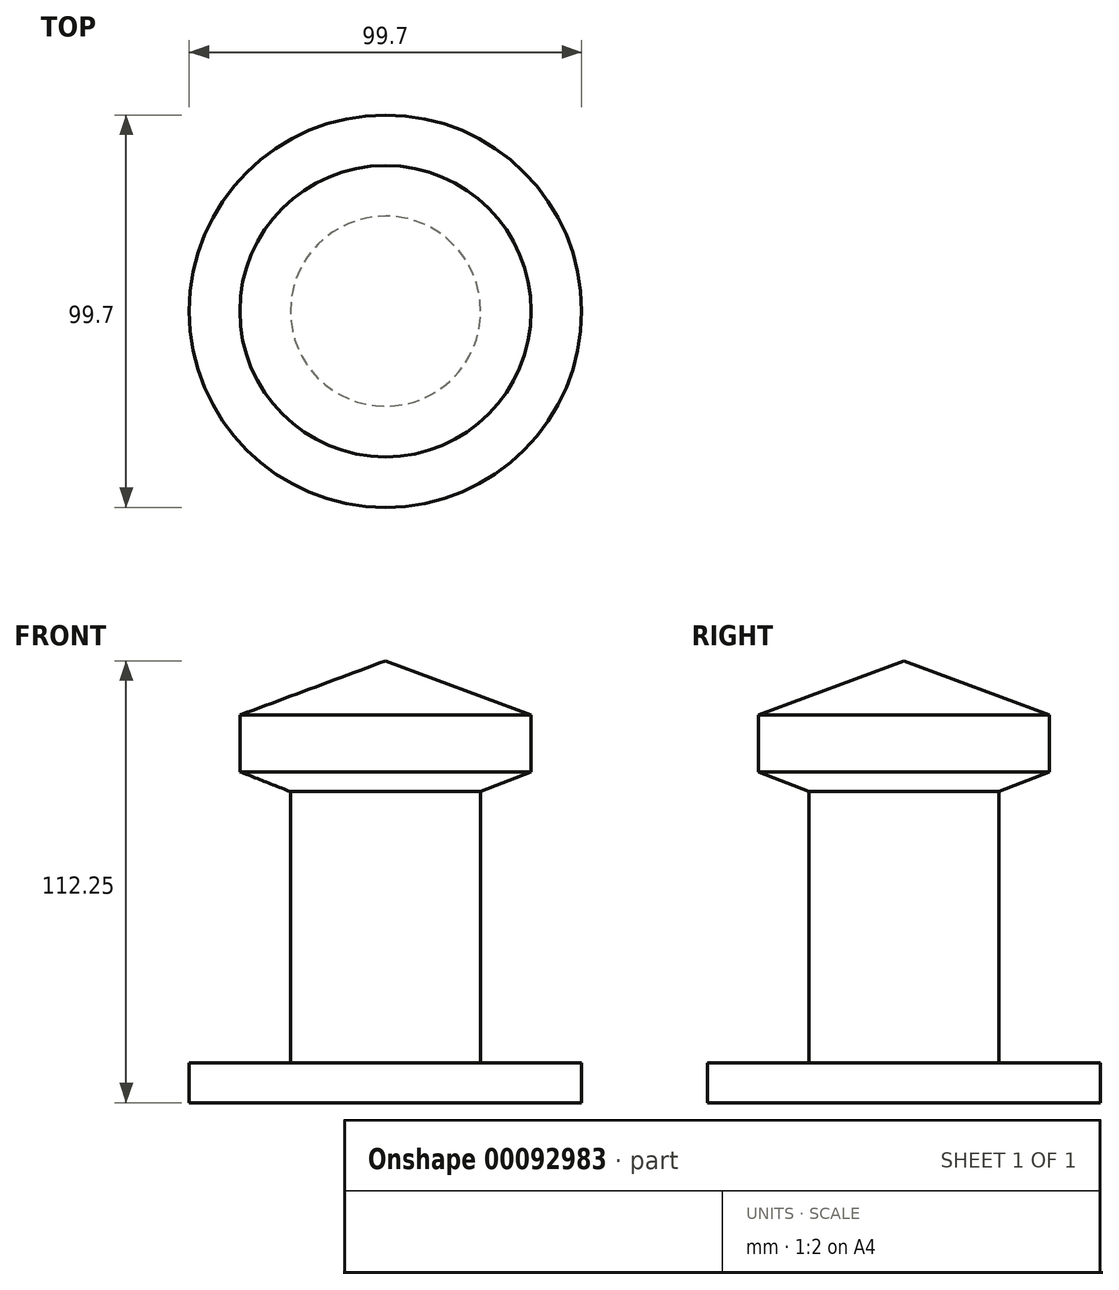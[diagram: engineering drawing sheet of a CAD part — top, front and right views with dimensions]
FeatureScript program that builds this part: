
annotation { "Feature Type Name" : "Feature", "Feature Type Description" : "" }
export const myFeature = defineFeature(function(context is Context, id is Id, definition is map)
    precondition{}
    {
        {
            var Q0;
            Q0=qCreatedBy(makeId("Front.planeOp"),FACE);
            var sketch = newSketch(context, id + "F0", { "sketchPlane" : qUnion([Q0])});
            skLineSegment(sketch, "E0", {"start": v(0, 57.22) * mm, "end": v(-37, 57.22) * mm});
            skLineSegment(sketch, "E1", {"start": v(-37, 57.22) * mm, "end": v(-37, 42.81) * mm});
            skLineSegment(sketch, "E2", {"start": v(-37, 42.81) * mm, "end": v(-24.16, 37.75) * mm});
            skLineSegment(sketch, "E3", {"start": v(-24.16, 37.75) * mm, "end": v(-24.16, -31.15) * mm});
            skLineSegment(sketch, "E4", {"start": v(-24.16, -31.15) * mm, "end": v(-49.85, -31.15) * mm});
            skLineSegment(sketch, "E5", {"start": v(-49.85, -31.15) * mm, "end": v(-49.85, -41.27) * mm});
            skLineSegment(sketch, "E6", {"start": v(-49.85, -41.27) * mm, "end": v(0, -41.27) * mm});
            skLineSegment(sketch, "E7", {"start": v(0, -41.27) * mm, "end": v(0, 57.22) * mm});
            skLineSegment(sketch, "E8", {"start": v(-37, 57.22) * mm, "end": v(0, 70.98) * mm});
            skLineSegment(sketch, "E9", {"start": v(0, 70.98) * mm, "end": v(0, 57.22) * mm});
            skSolve(sketch);
        }
        {
            var Q0;
            Q0 = qSketchRegion(id + "F0", true);
            var Q1;
            Q1=sQuery(id+"F0.wireOp",EDGE,"E7");
            revolve(context, id + "F1", {"entities" : qUnion([Q0]), "axis" : qUnion([Q1]), "revolveType" : RevolveType.FULL});
        }
    });
